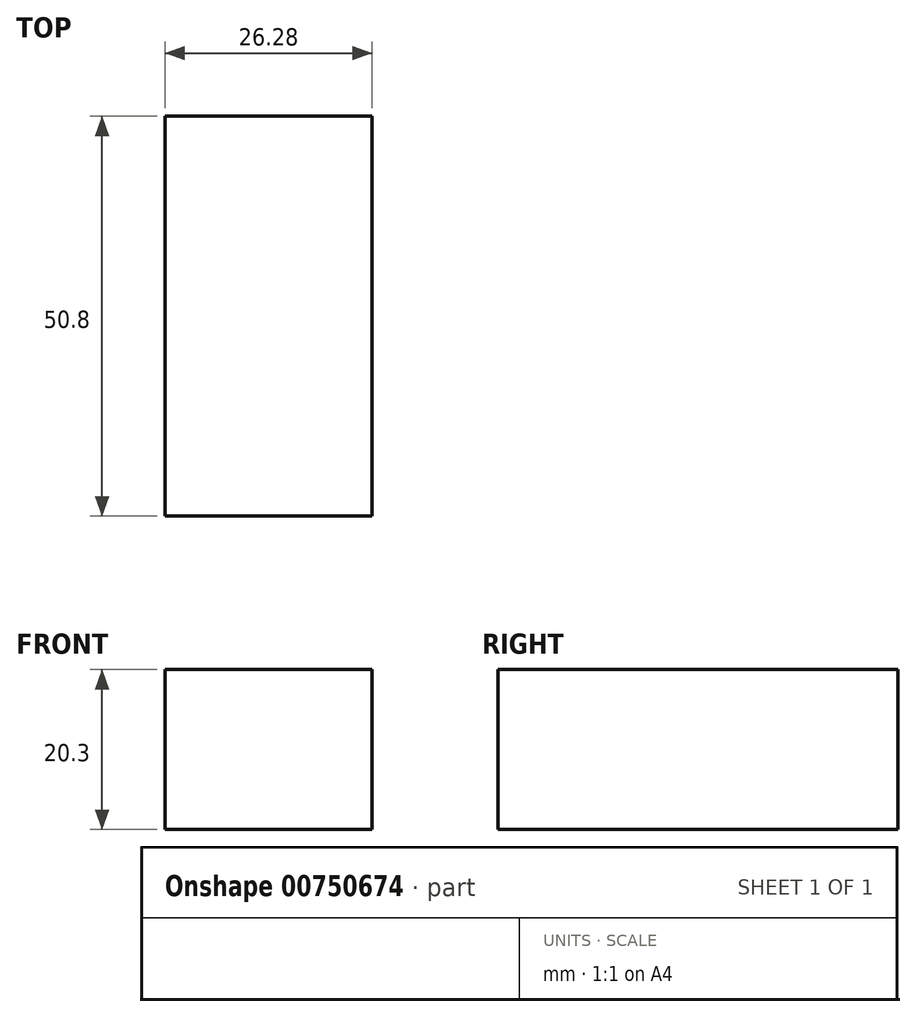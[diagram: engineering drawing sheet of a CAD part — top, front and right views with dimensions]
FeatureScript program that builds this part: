
annotation { "Feature Type Name" : "Feature", "Feature Type Description" : "" }
export const myFeature = defineFeature(function(context is Context, id is Id, definition is map)
    precondition{}
    {
        {
            var Q0;
            Q0=qCreatedBy(makeId("Front.planeOp"),FACE);
            var sketch = newSketch(context, id + "F0", { "sketchPlane" : qUnion([Q0])});
            skLineSegment(sketch, "E0.bottom", {"start": v(0, 0) * mm, "end": v(-26.28, 0) * mm});
            skLineSegment(sketch, "E0.top", {"start": v(0, -20.3) * mm, "end": v(-26.28, -20.3) * mm});
            skLineSegment(sketch, "E0.left", {"start": v(0, 0) * mm, "end": v(0, -20.3) * mm});
            skLineSegment(sketch, "E0.right", {"start": v(-26.28, 0) * mm, "end": v(-26.28, -20.3) * mm});
            skSolve(sketch);
        }
        {
            var Q0;
            Q0=makeQuery(id+"F0.imprint","IMPRINT",FACE,{"disambiguationData":[TD([[makeQuery(id+"F0.imprint","IMPRINT",EDGE,{"derivedFrom":sQuery(id+"F0.wireOp",EDGE,"E0.bottom")}),1.0]])]});
            extrude(context, id + "F1", {"entities" : qUnion([Q0]), "depth" : 50.8 * mm, "offsetDistance" : 25.4 * mm});
        }
    });
